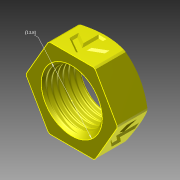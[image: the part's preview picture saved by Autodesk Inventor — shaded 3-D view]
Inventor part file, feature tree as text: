
AUTODESK INVENTOR PART (.ipt)
format: ipt  version: 2015 (Build 190159000, 159)  size: 1,209,856 bytes
history: native  units: in
note: dims shown in document units (in); Inventor stores cm internally (conversion verified against a paired STEP export)
features: sketch x3, other x1, imported_body x1, projected_geometry x1
ambient origin geometry x8: Origin, YZ Plane, XZ Plane, XY Plane, X Axis, Y Axis, Z Axis, Center Point
bodies: Solid1 (feature_tree)
feature tree (6):
  other  "TaperedNut1"
  sketch  "Sketch1"  dims[d0=0.5433in]
  sketch  "Sketch2"
  sketch  "Sketch3"
  imported_body  "Base1"
  projected_geometry  "Projected Loop1"
